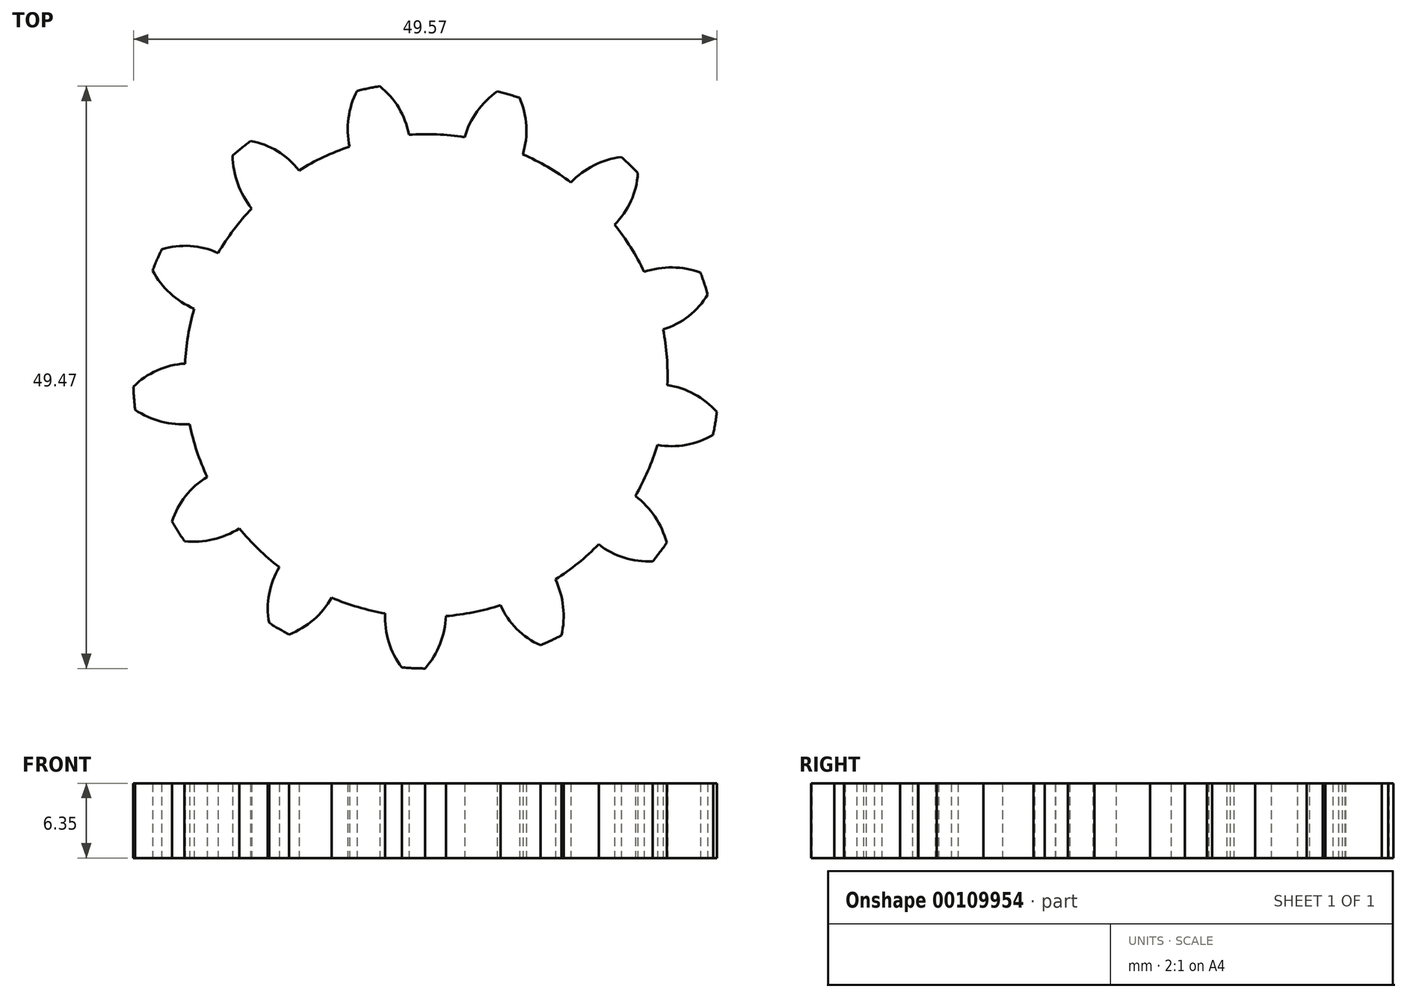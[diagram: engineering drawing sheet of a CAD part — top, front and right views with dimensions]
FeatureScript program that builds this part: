
annotation { "Feature Type Name" : "Feature", "Feature Type Description" : "" }
export const myFeature = defineFeature(function(context is Context, id is Id, definition is map)
    precondition{}
    {
        {
            var Q0;
            Q0=qCreatedBy(makeId("Top.planeOp"),FACE);
            var sketch = newSketch(context, id + "F0", { "sketchPlane" : qUnion([Q0])});
            skCircle(sketch, "E0", {"center": v(0, 0) * mm, "radius": 25.4 * mm, "construction": true});
            skCircle(sketch, "E1", {"center": v(0, 0) * mm, "radius": 24.9 * mm});
            skCircle(sketch, "E2", {"center": v(0, 0) * mm, "radius": 22.13 * mm, "construction": true});
            skCircle(sketch, "E3", {"center": v(0, 0) * mm, "radius": 20.9 * mm, "construction": true});
            skLineSegment(sketch, "E4", {"start": v(0, 20.9) * mm, "end": v(0, 25.4) * mm, "construction": true});
            skLineSegment(sketch, "E5", {"start": v(-6.36, 24.6) * mm, "end": v(-5.23, 20.23) * mm, "construction": true});
            skLineSegment(sketch, "E6", {"start": v(-5.23, 20.23) * mm, "end": v(0, 22.13) * mm, "construction": true});
            skLineSegment(sketch, "E7", {"start": v(-13.83, 20.7) * mm, "end": v(-14.11, 21.12) * mm});
            skLineSegment(sketch, "E8", {"start": v(0, 22.13) * mm, "end": v(6.63, 24.52) * mm, "construction": true});
            skLineSegment(sketch, "E9", {"start": v(10.24, 18.22) * mm, "end": v(3.9, 21.78) * mm, "construction": true});
            skCircle(sketch, "E10", {"center": v(10.24, 18.22) * mm, "radius": 7.26 * mm});
            skLineSegment(sketch, "E11", {"start": v(3.9, 21.78) * mm, "end": v(4.4, 24.5) * mm, "construction": true});
            skLineSegment(sketch, "E12", {"start": v(15.28, 19.65) * mm, "end": v(13.58, 17.47) * mm, "construction": true});
            skLineSegment(sketch, "E13", {"start": v(10.13, 22.74) * mm, "end": v(9, 20.21) * mm, "construction": true});
            skLineSegment(sketch, "E14", {"start": v(3.9, 21.78) * mm, "end": v(10.13, 22.74) * mm, "construction": true});
            skLineSegment(sketch, "E15", {"start": v(13.58, 17.47) * mm, "end": v(10.13, 22.74) * mm, "construction": true});
            skCircle(sketch, "E16", {"center": v(0, 0) * mm, "radius": 20.5 * mm});
            skLineSegment(sketch, "E17", {"start": v(5.68, 19.55) * mm, "end": v(3.26, 20.25) * mm, "construction": true});
            skLineSegment(sketch, "E18", {"start": v(9, 20.21) * mm, "end": v(8.5, 20.25) * mm});
            skLineSegment(sketch, "E19", {"start": v(8.5, 20.25) * mm, "end": v(1.77, 20.83) * mm, "construction": true});
            skCircle(sketch, "E20", {"center": v(1.77, 20.83) * mm, "radius": 6.75 * mm});
            skLineSegment(sketch, "E21", {"start": v(5.68, 19.55) * mm, "end": v(7.21, 24.82) * mm, "construction": true});
            skLineSegment(sketch, "E22", {"start": v(9, 20.21) * mm, "end": v(3.9, 21.78) * mm, "construction": true});
            skSolve(sketch);
        }
        {
            var Q0;
            {var subQ0=sQuery(id+"F0.wireOp",EDGE,"E20");var subQ3=sQuery(id+"F0.wireOp",EDGE,"E10");var subQ4=makeQuery(id+"F0.imprint","INTERSECT",VERTEX,{"disambiguationData":[OD(1.0)],"derivedFrom":[subQ3,subQ0]});Q0=makeQuery(id+"F0.imprint","IMPRINT",FACE,{"disambiguationData":[TD([[makeQuery(id+"F0.imprint","IMPRINT",EDGE,{"disambiguationData":[TD([[subQ4,-1.0]])],"derivedFrom":subQ3}),-1.0]])]});}
            var Q1;
            {var subQ0=sQuery(id+"F0.wireOp",EDGE,"E20");var subQ3=sQuery(id+"F0.wireOp",EDGE,"E10");var subQ4=makeQuery(id+"F0.imprint","INTERSECT",VERTEX,{"disambiguationData":[OD(1.0)],"derivedFrom":[subQ3,subQ0]});Q1=makeQuery(id+"F0.imprint","IMPRINT",FACE,{"disambiguationData":[TD([[makeQuery(id+"F0.imprint","IMPRINT",EDGE,{"disambiguationData":[TD([[subQ4,-1.0]])],"derivedFrom":subQ3}),1.0]])]});}
            var Q2;
            {var subQ1=sQuery(id+"F0.wireOp",EDGE,"E16");var subQ3=sQuery(id+"F0.wireOp",EDGE,"E10");var subQ5=makeQuery(id+"F0.imprint","INTERSECT",VERTEX,{"disambiguationData":[OD(0.0)],"derivedFrom":[subQ3,subQ1]});Q2=makeQuery(id+"F0.imprint","IMPRINT",FACE,{"disambiguationData":[TD([[makeQuery(id+"F0.imprint","IMPRINT",EDGE,{"disambiguationData":[TD([[subQ5,-1.0]])],"derivedFrom":subQ3}),1.0]])]});}
            var Q3;
            {var subQ1=sQuery(id+"F0.wireOp",EDGE,"E16");var subQ3=sQuery(id+"F0.wireOp",EDGE,"E10");var subQ5=makeQuery(id+"F0.imprint","INTERSECT",VERTEX,{"disambiguationData":[OD(0.0)],"derivedFrom":[subQ3,subQ1]});Q3=makeQuery(id+"F0.imprint","IMPRINT",FACE,{"disambiguationData":[TD([[makeQuery(id+"F0.imprint","IMPRINT",EDGE,{"disambiguationData":[TD([[subQ5,-1.0]])],"derivedFrom":subQ3}),-1.0]])]});}
            var Q4;
            {var subQ0=sQuery(id+"F0.wireOp",EDGE,"E20");var subQ3=makeQuery(id+"F0.imprint","IMPRINT",VERTEX,{"derivedFrom":subQ0});Q4=makeQuery(id+"F0.imprint","IMPRINT",FACE,{"disambiguationData":[TD([[makeQuery(id+"F0.imprint","IMPRINT",EDGE,{"disambiguationData":[TD([[subQ3,-1.0]])],"derivedFrom":subQ0}),1.0]])]});}
            extrude(context, id + "F1", {"entities" : qUnion([Q0, Q1, Q2, Q3, Q4]), "depth" : 6.35 * mm});
        }
        {
            var Q0;
            Q0=makeQuery(id+"F1.opExtrude","SWEPT_BODY",BODY,{"disambiguationData":[OSD([sQuery(id+"F0.wireOp",EDGE,"E1"),sQuery(id+"F0.wireOp",EDGE,"E10"),sQuery(id+"F0.wireOp",EDGE,"E16"),sQuery(id+"F0.wireOp",EDGE,"E20")])]});
            var Q1;
            Q1=makeQuery(id+"F1.opExtrude","CAP_EDGE",EDGE,{"disambiguationData":[OSD([sQuery(id+"F0.wireOp",EDGE,"E16")])],"isStart":false});
            circularPattern(context, id + "F2", {"operationType" : NewBodyOperationType.ADD, "entities" : qUnion([Q0]), "axis" : qUnion([Q1]), "angle" : 360 * degree, "instanceCount" : 13, "equalSpace" : true});
        }
    });
